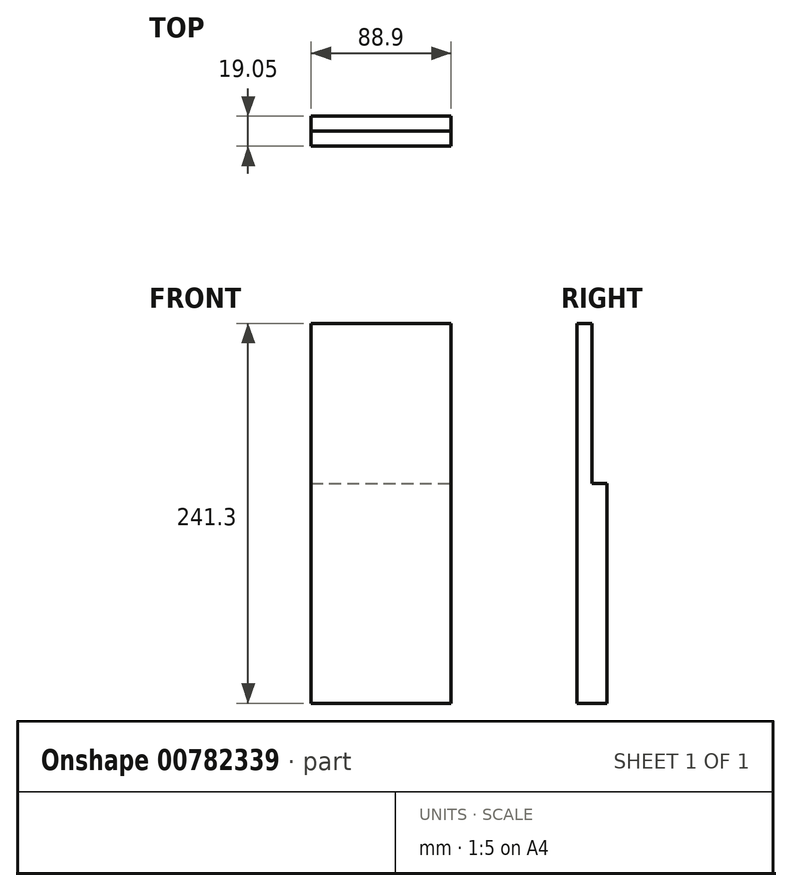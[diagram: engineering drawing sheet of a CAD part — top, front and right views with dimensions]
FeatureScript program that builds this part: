
annotation { "Feature Type Name" : "Feature", "Feature Type Description" : "" }
export const myFeature = defineFeature(function(context is Context, id is Id, definition is map)
    precondition{}
    {
        {
            var Q0;
            Q0=qCreatedBy(makeId("Front.planeOp"),FACE);
            var sketch = newSketch(context, id + "F0", { "sketchPlane" : qUnion([Q0])});
            skLineSegment(sketch, "E0.bottom", {"start": v(44.45, -120.65) * mm, "end": v(-44.45, -120.65) * mm});
            skLineSegment(sketch, "E0.top", {"start": v(44.45, 120.65) * mm, "end": v(-44.45, 120.65) * mm});
            skLineSegment(sketch, "E0.left", {"start": v(44.45, -120.65) * mm, "end": v(44.45, 120.65) * mm});
            skLineSegment(sketch, "E0.right", {"start": v(-44.45, -120.65) * mm, "end": v(-44.45, 120.65) * mm});
            skPoint(sketch, "E0.middle", {"position": v(0, 0) * mm});
            skSolve(sketch);
        }
        {
            var Q0;
            Q0 = qSketchRegion(id + "F0", true);
            extrude(context, id + "F1", {"entities" : qUnion([Q0]), "depth" : 19.05 * mm, "offsetDistance" : 25.4 * mm});
        }
        {
            var Q0;
            Q0=makeQuery(id+"F1.opExtrude","SWEPT_FACE",FACE,{"disambiguationData":[OSD([sQuery(id+"F0.wireOp",EDGE,"E0.left")])]});
            var sketch = newSketch(context, id + "F2", { "sketchPlane" : qUnion([Q0])});
            skLineSegment(sketch, "E1", {"start": v(-9.53, 120.65) * mm, "end": v(-9.53, 19.05) * mm});
            skLineSegment(sketch, "E2", {"start": v(-9.53, 19.05) * mm, "end": v(0, 19.05) * mm});
            skLineSegment(sketch, "E3", {"start": v(0, 19.05) * mm, "end": v(0, 120.65) * mm});
            skLineSegment(sketch, "E4", {"start": v(0, 120.65) * mm, "end": v(-9.53, 120.65) * mm});
            skSolve(sketch);
        }
        {
            var Q0;
            Q0 = qSketchRegion(id + "F2", true);
            extrude(context, id + "F3", {"entities" : qUnion([Q0]), "operationType" : NewBodyOperationType.REMOVE, "endBound" : BoundingType.UP_TO_NEXT, "oppositeDirection" : true, "depth" : 25.4 * mm, "offsetDistance" : 25.4 * mm});
        }
    });
